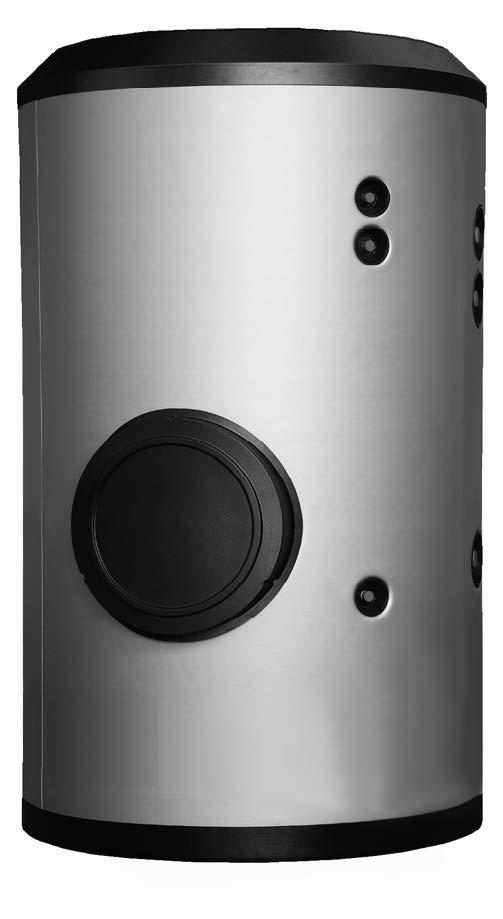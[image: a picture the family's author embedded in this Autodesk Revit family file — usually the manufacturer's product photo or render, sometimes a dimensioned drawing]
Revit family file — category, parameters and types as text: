
# Revit family: IMXV-2500SSB_CC01866
name_source: partatom
category: Aparatos eléctricos
revit_build: Autodesk Revit 2016 (Build: 20150220_1215(x64)
units: mm (PartAtom-declared; Revit-internal decimal feet)

## family parameters
Compartido = No
Corte con vacíos al cargar = No
Número OmniClass = 23.80.00.00
Punto de cálculo de habitación = No
Se basa en plano de trabajo = No
Siempre vertical = Sí
Título OmniClass = Electric Power and Lighting

## types (1)
- Depósitos gran capacidad IMXV-SB
    Clase eficiencia energética = C
    Costo = 0 $
    Código de montaje = CC01866
    Descripción = DEPÓSITOS GRAN CAPACIDAD VITRIFICADOS ACERO INOX.
    Dimensiones = 1660 x 2015 mm
    Fabricante = SALVADOR ESCODA
    Imagen de tipo = RB-IMXV.jpg
    Modelo = IMXV 2500 SSB
    Peso en vacío = 584 Kg
    Presión máx. circuito = 25 bar
    Presión máx. depósito = 8 bar
    Superfície intercambio = 6,1 m2
    Temperatura máx. ACS = 90 ºC
    Temperatura máx. circuito = 120 ºC
    URL = www.salvadorescoda.com
    Volúmen = 2500 l
